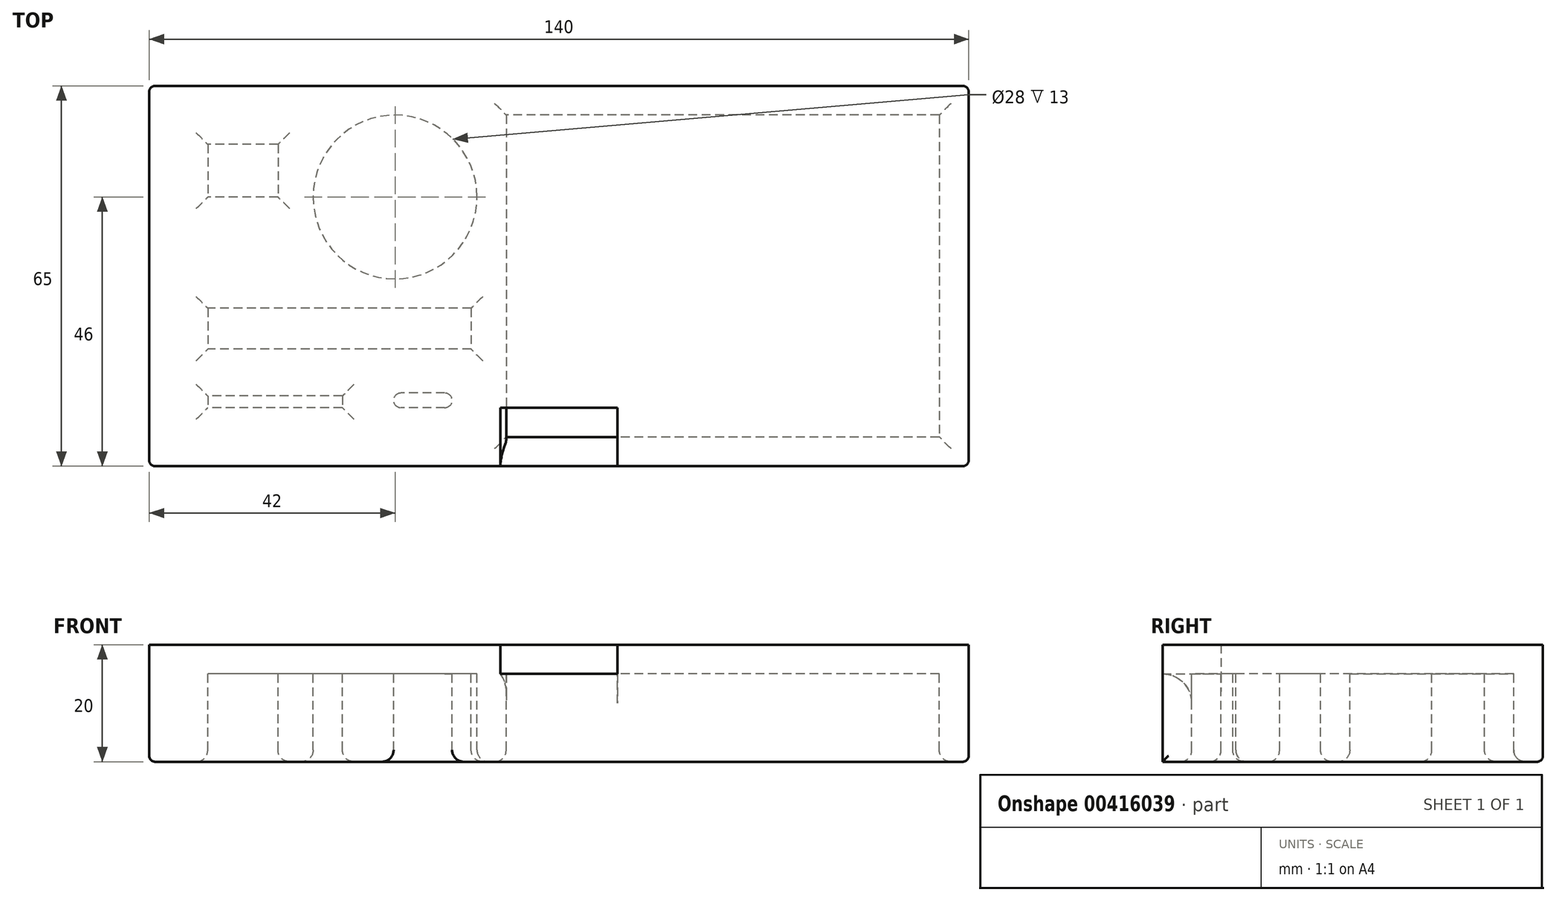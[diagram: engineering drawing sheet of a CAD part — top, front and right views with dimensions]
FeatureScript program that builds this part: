
annotation { "Feature Type Name" : "Feature", "Feature Type Description" : "" }
export const myFeature = defineFeature(function(context is Context, id is Id, definition is map)
    precondition{}
    {
        {
            var Q0;
            Q0=qCreatedBy(makeId("Top.planeOp"),FACE);
            var sketch = newSketch(context, id + "F0", { "sketchPlane" : qUnion([Q0])});
            skLineSegment(sketch, "E0.bottom", {"start": v(0, 0) * mm, "end": v(140, 0) * mm});
            skLineSegment(sketch, "E0.top", {"start": v(0, 65) * mm, "end": v(140, 65) * mm});
            skLineSegment(sketch, "E0.left", {"start": v(0, 0) * mm, "end": v(0, 65) * mm});
            skLineSegment(sketch, "E0.right", {"start": v(140, 0) * mm, "end": v(140, 65) * mm});
            skLineSegment(sketch, "E1.bottom", {"start": v(60, 0) * mm, "end": v(80, 0) * mm});
            skLineSegment(sketch, "E1.top", {"start": v(60, 10) * mm, "end": v(80, 10) * mm});
            skLineSegment(sketch, "E1.left", {"start": v(60, 0) * mm, "end": v(60, 10) * mm});
            skLineSegment(sketch, "E1.right", {"start": v(80, 0) * mm, "end": v(80, 10) * mm});
            skSolve(sketch);
        }
        {
            var Q0;
            Q0=makeQuery(id+"F0.imprint","IMPRINT",FACE,{"disambiguationData":[TD([[makeQuery(id+"F0.imprint","IMPRINT",EDGE,{"derivedFrom":sQuery(id+"F0.wireOp",EDGE,"E0.top")}),-1.0]])]});
            extrude(context, id + "F1", {"entities" : qUnion([Q0]), "depth" : 3 * mm});
        }
        {
            var Q0;
            Q0=makeQuery(id+"F1.opExtrude","CAP_FACE",FACE,{"disambiguationData":[OSD([sQuery(id+"F0.wireOp",EDGE,"E0.bottom"),sQuery(id+"F0.wireOp",EDGE,"E0.top"),sQuery(id+"F0.wireOp",EDGE,"E0.left"),sQuery(id+"F0.wireOp",EDGE,"E0.right"),sQuery(id+"F0.wireOp",EDGE,"E1.top"),sQuery(id+"F0.wireOp",EDGE,"E1.left"),sQuery(id+"F0.wireOp",EDGE,"E1.right")])],"isStart":false});
            var Q1;
            Q1=makeQuery(id+"F0.imprint","IMPRINT",FACE,{"disambiguationData":[TD([[makeQuery(id+"F0.imprint","IMPRINT",EDGE,{"derivedFrom":sQuery(id+"F0.wireOp",EDGE,"E1.bottom")}),1.0]])]});
            extrude(context, id + "F2", {"entities" : qUnion([Q0, Q1]), "operationType" : NewBodyOperationType.ADD, "depth" : 2 * mm});
        }
        {
            var Q0;
            Q0=makeQuery(id+"F0.imprint","IMPRINT",FACE,{"disambiguationData":[TD([[makeQuery(id+"F0.imprint","IMPRINT",EDGE,{"derivedFrom":sQuery(id+"F0.wireOp",EDGE,"E0.top")}),-1.0]])]});
            var sketch = newSketch(context, id + "F3", { "sketchPlane" : qUnion([Q0])});
            skLineSegment(sketch, "E2.bottom", {"start": v(55, 27) * mm, "end": v(10, 27) * mm});
            skLineSegment(sketch, "E2.top", {"start": v(55, 20) * mm, "end": v(10, 20) * mm});
            skLineSegment(sketch, "E2.left", {"start": v(55, 27) * mm, "end": v(55, 20) * mm});
            skLineSegment(sketch, "E2.right", {"start": v(10, 27) * mm, "end": v(10, 20) * mm});
            skLineSegment(sketch, "E3.bottom", {"start": v(22, 55) * mm, "end": v(10, 55) * mm});
            skLineSegment(sketch, "E3.top", {"start": v(22, 46) * mm, "end": v(10, 46) * mm});
            skLineSegment(sketch, "E3.left", {"start": v(22, 55) * mm, "end": v(22, 46) * mm});
            skLineSegment(sketch, "E3.right", {"start": v(10, 55) * mm, "end": v(10, 46) * mm});
            skLineSegment(sketch, "E4.bottom", {"start": v(33, 12) * mm, "end": v(10, 12) * mm});
            skLineSegment(sketch, "E4.top", {"start": v(33, 10) * mm, "end": v(11.25, 10) * mm});
            skLineSegment(sketch, "E4.left", {"start": v(33, 12) * mm, "end": v(33, 10) * mm});
            skLineSegment(sketch, "E4.right", {"start": v(10, 12) * mm, "end": v(10, 11.25) * mm});
            skLineSegment(sketch, "E5.bottom", {"start": v(50.5, 12.5) * mm, "end": v(43, 12.5) * mm});
            skLineSegment(sketch, "E5.top", {"start": v(50.5, 10) * mm, "end": v(43, 10) * mm});
            skLineSegment(sketch, "E5.left", {"start": v(51.75, 11.25) * mm, "end": v(51.75, 11.25) * mm});
            skLineSegment(sketch, "E5.right", {"start": v(41.75, 11.25) * mm, "end": v(41.75, 11.25) * mm});
            skCircle(sketch, "E6", {"center": v(42, 46) * mm, "radius": 14 * mm});
            skPoint(sketch, "E7.visualSharp", {"position": v(41.75, 12.5) * mm});
            skArc(sketch, "E7.filletArc", {"start": v(43, 12.5) * mm, "mid": v(42.12, 12.13) * mm, "end": v(41.75, 11.25) * mm});
            skPoint(sketch, "E8.visualSharp", {"position": v(41.75, 10) * mm});
            skArc(sketch, "E8.filletArc", {"start": v(41.75, 11.25) * mm, "mid": v(42.12, 10.37) * mm, "end": v(43, 10) * mm});
            skPoint(sketch, "E9.visualSharp", {"position": v(51.75, 10) * mm});
            skArc(sketch, "E9.filletArc", {"start": v(50.5, 10) * mm, "mid": v(51.38, 10.37) * mm, "end": v(51.75, 11.25) * mm});
            skPoint(sketch, "E10.visualSharp", {"position": v(51.75, 12.5) * mm});
            skArc(sketch, "E10.filletArc", {"start": v(51.75, 11.25) * mm, "mid": v(51.38, 12.13) * mm, "end": v(50.5, 12.5) * mm});
            skPoint(sketch, "E11.visualSharp", {"position": v(10, 10) * mm});
            skLineSegment(sketch, "E12.bottom", {"start": v(135, 60) * mm, "end": v(61, 60) * mm});
            skLineSegment(sketch, "E12.top", {"start": v(135, 5) * mm, "end": v(61, 5) * mm});
            skLineSegment(sketch, "E12.left", {"start": v(135, 60) * mm, "end": v(135, 5) * mm});
            skLineSegment(sketch, "E12.right", {"start": v(61, 60) * mm, "end": v(61, 5) * mm});
            skLineSegment(sketch, "E13.0", {"start": v(0, 0) * mm, "end": v(140, 0) * mm});
            skLineSegment(sketch, "E14.0.0", {"start": v(0, 0) * mm, "end": v(0, 65) * mm});
            skLineSegment(sketch, "E14.0.1", {"start": v(0, 65) * mm, "end": v(140, 65) * mm});
            skLineSegment(sketch, "E14.0.2", {"start": v(140, 65) * mm, "end": v(140, 0) * mm});
            skLineSegment(sketch, "E14.0.3", {"start": v(140, 0) * mm, "end": v(0, 0) * mm});
            skLineSegment(sketch, "E15", {"start": v(11.25, 10) * mm, "end": v(10, 10) * mm});
            skLineSegment(sketch, "E16", {"start": v(10, 11.25) * mm, "end": v(10, 10) * mm});
            skSolve(sketch);
        }
        {
            var Q0;
            {var subQ0=sQuery(id+"F3.wireOp",EDGE,"E12.top");var subQ1=makeQuery(id+"F0.imprint","IMPRINT",EDGE,{"derivedFrom":sQuery(id+"F0.wireOp",EDGE,"E1.right")});var subQ2=makeQuery(id+"F3.imprint","INTERSECT",VERTEX,{"derivedFrom":[subQ1,subQ0]});Q0=makeQuery(id+"F3.imprint","IMPRINT",FACE,{"disambiguationData":[TD([[makeQuery(id+"F3.imprint","IMPRINT",EDGE,{"disambiguationData":[TD([[subQ2,-1.0]])],"derivedFrom":subQ0}),1.0]])]});}
            var Q1;
            Q1=makeQuery(id+"F3.imprint","IMPRINT",FACE,{"disambiguationData":[TD([[makeQuery(id+"F3.imprint","IMPRINT",EDGE,{"derivedFrom":sQuery(id+"F3.wireOp",EDGE,"E2.bottom")}),-1.0]])]});
            extrude(context, id + "F4", {"entities" : qUnion([Q0, Q1]), "operationType" : NewBodyOperationType.ADD, "oppositeDirection" : true, "depth" : 15 * mm});
        }
        {
            var Q0;
            Q0=makeQuery(id+"F4.opExtrude","CAP_EDGE",EDGE,{"disambiguationData":[OSD([sQuery(id+"F3.wireOp",EDGE,"E12.bottom")])],"isStart":true});
            var Q1;
            Q1=makeQuery(id+"F4.opExtrude","CAP_EDGE",EDGE,{"disambiguationData":[OSD([sQuery(id+"F3.wireOp",EDGE,"E12.right")])],"isStart":true});
            var Q2;
            Q2=makeQuery(id+"F4.opExtrude","CAP_EDGE",EDGE,{"disambiguationData":[OSD([sQuery(id+"F3.wireOp",EDGE,"E12.top")])],"isStart":true});
            var Q3;
            {var subQ0=sQuery(id+"F0.wireOp",EDGE,"E1.right");var subQ1=sQuery(id+"F0.wireOp",EDGE,"E1.left");var subQ2=sQuery(id+"F0.wireOp",EDGE,"E1.top");Q3=makeQuery(id+"F4.boolean.opBoolean","SPLIT",FACE,{"disambiguationData":[TD([makeQuery(id+"F4.opExtrude","SWEPT_FACE",FACE,{"disambiguationData":[OSD([sQuery(id+"F3.wireOp",EDGE,"E12.bottom")])]})])],"derivedFrom":makeQuery(id+"F2.boolean.opBoolean","MERGE",FACE,{"derivedFrom":[makeQuery(id+"F1.opExtrude","CAP_FACE",FACE,{"disambiguationData":[OSD([sQuery(id+"F0.wireOp",EDGE,"E0.bottom"),sQuery(id+"F0.wireOp",EDGE,"E0.top"),sQuery(id+"F0.wireOp",EDGE,"E0.left"),sQuery(id+"F0.wireOp",EDGE,"E0.right"),subQ2,subQ1,subQ0])],"isStart":true}),makeQuery(id+"F2.opExtrude","CAP_FACE",FACE,{"disambiguationData":[OSD([sQuery(id+"F0.wireOp",EDGE,"E1.bottom"),subQ2,subQ1,subQ0])],"isStart":true})]})});}
            fillet(context, id + "F5", {"entities" : qUnion([Q0, Q1, Q2, Q3]), "radius" : 5 * mm, "tangentPropagation" : true, "allowEdgeOverflow" : false});
        }
        {
            var Q0;
            Q0=makeQuery(id+"F4.opExtrude","CAP_EDGE",EDGE,{"disambiguationData":[OSD([sQuery(id+"F3.wireOp",EDGE,"E12.bottom")])],"isStart":false});
            var Q1;
            Q1=makeQuery(id+"F4.opExtrude","CAP_EDGE",EDGE,{"disambiguationData":[OSD([sQuery(id+"F3.wireOp",EDGE,"E12.left")])],"isStart":false});
            var Q2;
            Q2=makeQuery(id+"F4.opExtrude","CAP_EDGE",EDGE,{"disambiguationData":[OSD([sQuery(id+"F3.wireOp",EDGE,"E12.top")])],"isStart":false});
            var Q3;
            Q3=makeQuery(id+"F4.opExtrude","CAP_EDGE",EDGE,{"disambiguationData":[OSD([sQuery(id+"F3.wireOp",EDGE,"E12.right")])],"isStart":false});
            var Q4;
            Q4=makeQuery(id+"F4.opExtrude","CAP_EDGE",EDGE,{"disambiguationData":[OSD([sQuery(id+"F3.wireOp",EDGE,"E6")])],"isStart":false});
            var Q5;
            Q5=makeQuery(id+"F4.opExtrude","CAP_EDGE",EDGE,{"disambiguationData":[OSD([sQuery(id+"F3.wireOp",EDGE,"E3.bottom")])],"isStart":false});
            var Q6;
            Q6=makeQuery(id+"F4.opExtrude","CAP_EDGE",EDGE,{"disambiguationData":[OSD([sQuery(id+"F3.wireOp",EDGE,"E3.right")])],"isStart":false});
            var Q7;
            Q7=makeQuery(id+"F4.opExtrude","CAP_EDGE",EDGE,{"disambiguationData":[OSD([sQuery(id+"F3.wireOp",EDGE,"E3.top")])],"isStart":false});
            var Q8;
            Q8=makeQuery(id+"F4.opExtrude","CAP_EDGE",EDGE,{"disambiguationData":[OSD([sQuery(id+"F3.wireOp",EDGE,"E3.left")])],"isStart":false});
            var Q9;
            Q9=makeQuery(id+"F4.opExtrude","CAP_EDGE",EDGE,{"disambiguationData":[OSD([sQuery(id+"F3.wireOp",EDGE,"E2.bottom")])],"isStart":false});
            var Q10;
            Q10=makeQuery(id+"F4.opExtrude","CAP_EDGE",EDGE,{"disambiguationData":[OSD([sQuery(id+"F3.wireOp",EDGE,"E2.right")])],"isStart":false});
            var Q11;
            Q11=makeQuery(id+"F4.opExtrude","CAP_EDGE",EDGE,{"disambiguationData":[OSD([sQuery(id+"F3.wireOp",EDGE,"E2.top")])],"isStart":false});
            var Q12;
            Q12=makeQuery(id+"F4.opExtrude","CAP_EDGE",EDGE,{"disambiguationData":[OSD([sQuery(id+"F3.wireOp",EDGE,"E2.left")])],"isStart":false});
            var Q13;
            Q13=makeQuery(id+"F4.opExtrude","CAP_EDGE",EDGE,{"disambiguationData":[OSD([sQuery(id+"F3.wireOp",EDGE,"E5.bottom")])],"isStart":false});
            var Q14;
            Q14=makeQuery(id+"F4.opExtrude","CAP_EDGE",EDGE,{"disambiguationData":[OSD([sQuery(id+"F3.wireOp",EDGE,"E4.top")])],"isStart":false});
            var Q15;
            Q15=makeQuery(id+"F4.opExtrude","CAP_EDGE",EDGE,{"disambiguationData":[OSD([sQuery(id+"F3.wireOp",EDGE,"E4.left")])],"isStart":false});
            var Q16;
            Q16=makeQuery(id+"F4.opExtrude","CAP_EDGE",EDGE,{"disambiguationData":[OSD([sQuery(id+"F3.wireOp",EDGE,"E4.bottom")])],"isStart":false});
            var Q17;
            Q17=makeQuery(id+"F4.opExtrude","CAP_EDGE",EDGE,{"disambiguationData":[OSD([sQuery(id+"F3.wireOp",EDGE,"E4.right"),sQuery(id+"F3.wireOp",EDGE,"E16")])],"isStart":false});
            fillet(context, id + "F6", {"entities" : qUnion([Q0, Q1, Q2, Q3, Q4, Q5, Q6, Q7, Q8, Q9, Q10, Q11, Q12, Q13, Q14, Q15, Q16, Q17]), "radius" : 2 * mm, "tangentPropagation" : true, "allowEdgeOverflow" : false});
        }
        {
            var Q0;
            Q0=makeQuery(id+"F4.opExtrude","CAP_EDGE",EDGE,{"disambiguationData":[OSD([sQuery(id+"F3.wireOp",EDGE,"E14.0.2")])],"isStart":false});
            var Q1;
            Q1=makeQuery(id+"F4.opExtrude","CAP_EDGE",EDGE,{"disambiguationData":[OSD([sQuery(id+"F3.wireOp",EDGE,"E14.0.1")])],"isStart":false});
            var Q2;
            Q2=makeQuery(id+"F4.opExtrude","CAP_EDGE",EDGE,{"disambiguationData":[OSD([sQuery(id+"F3.wireOp",EDGE,"E14.0.0")])],"isStart":false});
            var Q3;
            Q3=makeQuery(id+"F4.opExtrude","CAP_EDGE",EDGE,{"disambiguationData":[OSD([sQuery(id+"F3.wireOp",EDGE,"E14.0.3")])],"isStart":false});
            var Q4;
            {var subQ0=sQuery(id+"F0.wireOp",EDGE,"E0.left");var subQ1=sQuery(id+"F0.wireOp",EDGE,"E0.bottom");Q4=makeQuery(id+"F4.boolean.opBoolean","MERGE",EDGE,{"derivedFrom":[makeQuery(id+"F2.boolean.opBoolean","MERGE",EDGE,{"derivedFrom":[makeQuery(id+"F1.opExtrude","SWEPT_EDGE",EDGE,{"disambiguationData":[OSD([subQ1,subQ0])]}),makeQuery(id+"F2.opExtrude","SWEPT_EDGE",EDGE,{"disambiguationData":[OSD([subQ1,subQ0])]})]}),makeQuery(id+"F4.opExtrude","SWEPT_EDGE",EDGE,{"disambiguationData":[OSD([sQuery(id+"F3.wireOp",EDGE,"E14.0.0"),sQuery(id+"F3.wireOp",EDGE,"E14.0.3")])]})]});}
            var Q5;
            {var subQ0=sQuery(id+"F0.wireOp",EDGE,"E0.right");var subQ1=sQuery(id+"F0.wireOp",EDGE,"E0.bottom");Q5=makeQuery(id+"F4.boolean.opBoolean","MERGE",EDGE,{"derivedFrom":[makeQuery(id+"F2.boolean.opBoolean","MERGE",EDGE,{"derivedFrom":[makeQuery(id+"F1.opExtrude","SWEPT_EDGE",EDGE,{"disambiguationData":[OSD([subQ1,subQ0])]}),makeQuery(id+"F2.opExtrude","SWEPT_EDGE",EDGE,{"disambiguationData":[OSD([subQ1,subQ0])]})]}),makeQuery(id+"F4.opExtrude","SWEPT_EDGE",EDGE,{"disambiguationData":[OSD([sQuery(id+"F3.wireOp",EDGE,"E14.0.2"),sQuery(id+"F3.wireOp",EDGE,"E14.0.3")])]})]});}
            var Q6;
            {var subQ0=sQuery(id+"F0.wireOp",EDGE,"E0.right");var subQ1=sQuery(id+"F0.wireOp",EDGE,"E0.top");Q6=makeQuery(id+"F4.boolean.opBoolean","MERGE",EDGE,{"derivedFrom":[makeQuery(id+"F2.boolean.opBoolean","MERGE",EDGE,{"derivedFrom":[makeQuery(id+"F1.opExtrude","SWEPT_EDGE",EDGE,{"disambiguationData":[OSD([subQ1,subQ0])]}),makeQuery(id+"F2.opExtrude","SWEPT_EDGE",EDGE,{"disambiguationData":[OSD([subQ1,subQ0])]})]}),makeQuery(id+"F4.opExtrude","SWEPT_EDGE",EDGE,{"disambiguationData":[OSD([sQuery(id+"F3.wireOp",EDGE,"E14.0.1"),sQuery(id+"F3.wireOp",EDGE,"E14.0.2")])]})]});}
            var Q7;
            {var subQ0=sQuery(id+"F0.wireOp",EDGE,"E0.left");var subQ1=sQuery(id+"F0.wireOp",EDGE,"E0.top");Q7=makeQuery(id+"F4.boolean.opBoolean","MERGE",EDGE,{"derivedFrom":[makeQuery(id+"F2.boolean.opBoolean","MERGE",EDGE,{"derivedFrom":[makeQuery(id+"F1.opExtrude","SWEPT_EDGE",EDGE,{"disambiguationData":[OSD([subQ1,subQ0])]}),makeQuery(id+"F2.opExtrude","SWEPT_EDGE",EDGE,{"disambiguationData":[OSD([subQ1,subQ0])]})]}),makeQuery(id+"F4.opExtrude","SWEPT_EDGE",EDGE,{"disambiguationData":[OSD([sQuery(id+"F3.wireOp",EDGE,"E14.0.0"),sQuery(id+"F3.wireOp",EDGE,"E14.0.1")])]})]});}
            fillet(context, id + "F7", {"entities" : qUnion([Q0, Q1, Q2, Q3, Q4, Q5, Q6, Q7]), "radius" : 1 * mm, "tangentPropagation" : true, "allowEdgeOverflow" : false});
        }
    });
